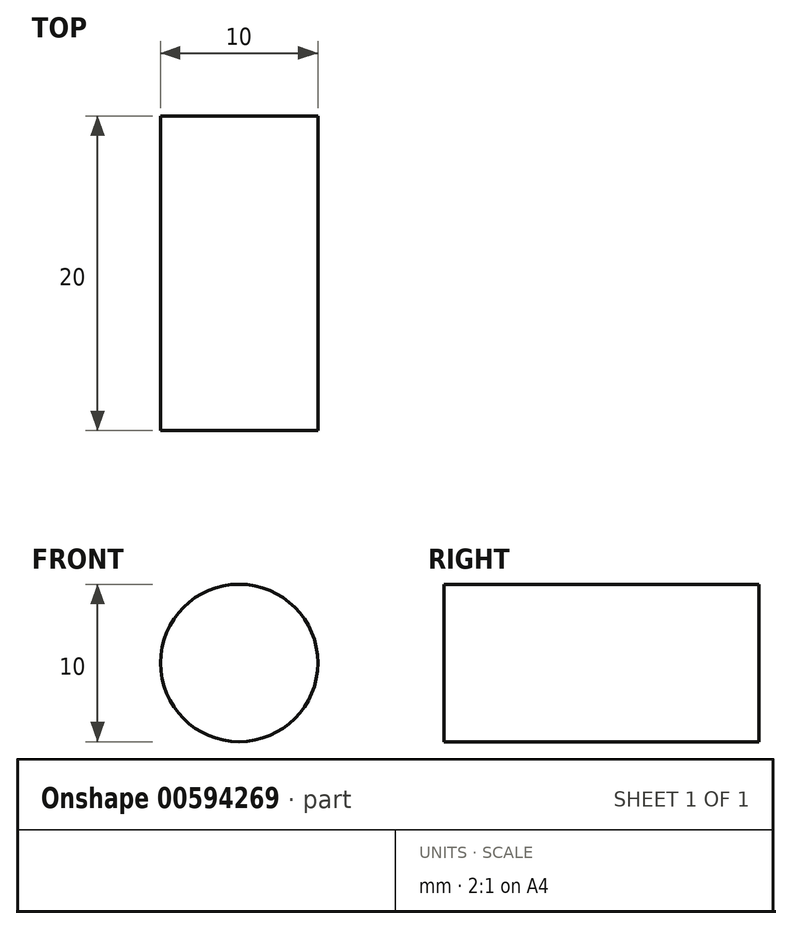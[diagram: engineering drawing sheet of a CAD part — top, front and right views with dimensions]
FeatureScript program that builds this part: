
annotation { "Feature Type Name" : "Feature", "Feature Type Description" : "" }
export const myFeature = defineFeature(function(context is Context, id is Id, definition is map)
    precondition{}
    {
        {
            var Q0;
            Q0=qCreatedBy(makeId("Front.planeOp"),FACE);
            var sketch = newSketch(context, id + "F0", { "sketchPlane" : qUnion([Q0])});
            skCircle(sketch, "E0", {"center": v(0, 0) * mm, "radius": 5 * mm});
            skSolve(sketch);
        }
        {
            var Q0;
            Q0 = qSketchRegion(id + "F0", true);
            extrude(context, id + "F1", {"entities" : qUnion([Q0]), "depth" : 20 * mm, "offsetDistance" : 25 * mm});
        }
    });
